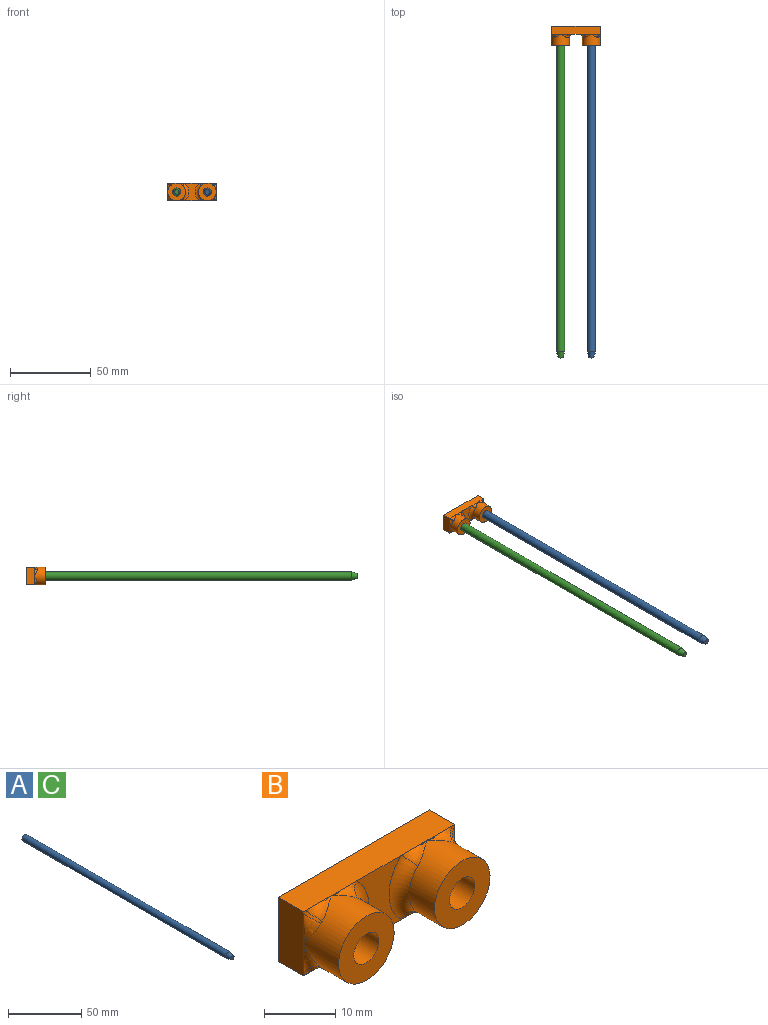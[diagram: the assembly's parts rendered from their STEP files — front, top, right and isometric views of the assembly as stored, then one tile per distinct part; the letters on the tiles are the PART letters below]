
ASSEMBLY  parts=3 mates=2
PART A: 4 faces, bbox 5x200x5 mm
  f0: cylinder r=2.5mm len=196mm, axis (0,1,0), area 3078.8mm2, adj f2,f3
  f1: plane 3x3mm, normal (0,-1,0), area 7.1mm2, adj f3
  f2: plane 5x5mm, normal (0,1,0), area 19.6mm2, adj f0
  f3: cone r=1.5mm half-angle=14deg, axis (0,1,0), area 51.8mm2, adj f0,f1
PART B: 36 faces, bbox 32.3x12.2x14.3 mm
  f0: plane 11x8.8mm, normal (0,-1,0), area 60.3mm2, adj f4,f6,f28,f31
  f1: plane 0.4x0.4mm, normal (0,-1,0), area 0.1mm2, adj f4,f7,f22
  f2: plane 0.4x0.4mm, normal (0,-1,0), area 0.1mm2, adj f5,f6,f25
  f3: plane 0.4x0.4mm, normal (0,-1,0), area 0.1mm2, adj f4,f5,f34
  f4: plane 30x5mm, normal (0,0,1), area 150mm2, adj f0,f1,f3,f5,f7,f9,f23,f29
  f5: plane 11.19x5.19mm, normal (-1,0,0), area 55mm2, adj f2,f3,f4,f6,f9,f24,f35
  f6: plane 30x5mm, normal (0,0,-1), area 150mm2, adj f0,f2,f5,f7,f8,f9,f18,f26
  f7: plane 11.19x5.19mm, normal (1,0,0), area 55mm2, adj f1,f4,f6,f8,f9,f20,f21
  f8: plane 0.4x0.4mm, normal (0,-1,0), area 0.1mm2, adj f6,f7,f19
  f9: plane 30x11mm, normal (0,1,0), area 330mm2, adj f4,f5,f6,f7
  f10: cylinder r=2.5mm len=7mm, axis (0,1,0), area 110mm2, adj f12,f13
  f11: cylinder r=5.5mm len=11mm, axis (0,1,0), area 191.8mm2, adj f12,f24,f25,f26,f27,f28,f29,f33
  f12: plane 11x11mm, normal (0,-1,0), area 75.4mm2, adj f10,f11
  f13: plane 5x5mm, normal (0,-1,0), area 19.6mm2, adj f10
  f14: cylinder r=2.5mm len=7mm, axis (0,1,0), area 110mm2, adj f16,f17
  f15: cylinder r=5.5mm len=11mm, axis (0,1,0), area 191.8mm2, adj f16,f18,f19,f20,f21,f22,f23,f30
  f16: plane 11x11mm, normal (0,-1,0), area 75.4mm2, adj f14,f15
  f17: plane 5x5mm, normal (0,-1,0), area 19.6mm2, adj f14
  f18: bspline ~5.28x2.12mm, area 6.4mm2, adj f6,f15,f19
  f19: torus R=7.5mm, axis (0,-1,0), area 1.5mm2, adj f8,f15,f18,f20
  f20: bspline ~5.28x2.12mm, area 6.2mm2, adj f7,f15,f19
  f21: bspline ~5.28x2.12mm, area 6.2mm2, adj f7,f15,f22
  f22: torus R=7.5mm, axis (0,-1,0), area 1.5mm2, adj f1,f15,f21,f23
  f23: bspline ~5.28x2.12mm, area 6.4mm2, adj f4,f15,f22
  f24: bspline ~5.28x2.12mm, area 6.4mm2, adj f5,f11,f25
  f25: torus R=7.5mm, axis (0,-1,0), area 1.5mm2, adj f2,f11,f24,f26
  f26: bspline ~5.28x2.12mm, area 6.4mm2, adj f6,f11,f25
  f27: bspline ~5.1x2mm, area 6.4mm2, adj f6,f11,f28
  f28: torus R=7.5mm, axis (0,-1,0), area 32.2mm2, adj f0,f11,f27,f29
  f29: bspline ~5.28x2.12mm, area 6.4mm2, adj f4,f11,f28
  f30: bspline ~5.1x2mm, area 6.4mm2, adj f4,f15,f31
  f31: torus R=7.5mm, axis (0,-1,0), area 32.2mm2, adj f0,f15,f30,f32
  f32: bspline ~5.28x2.12mm, area 6.4mm2, adj f6,f15,f31
  f33: bspline ~5.28x2.12mm, area 6.4mm2, adj f4,f11,f34
  f34: torus R=7.5mm, axis (0,-1,0), area 1.5mm2, adj f3,f11,f33,f35
  f35: bspline ~5.28x2.12mm, area 6.2mm2, adj f5,f11,f34
PART C: same geometry as A
PLACE A t=(9.57,0.98,-0.09)mm
PLACE B t=(0.07,5.98,-0.09)mm fixed
PLACE C t=(-9.43,0.98,-0.09)mm
MATE fastened C.f0 <-> B.f10  axis (0,1,0) through (-9.43,0.98,-0.09)mm
MATE fastened A.f0 <-> B.f14  axis (0,1,0) through (9.57,0.98,-0.09)mm
